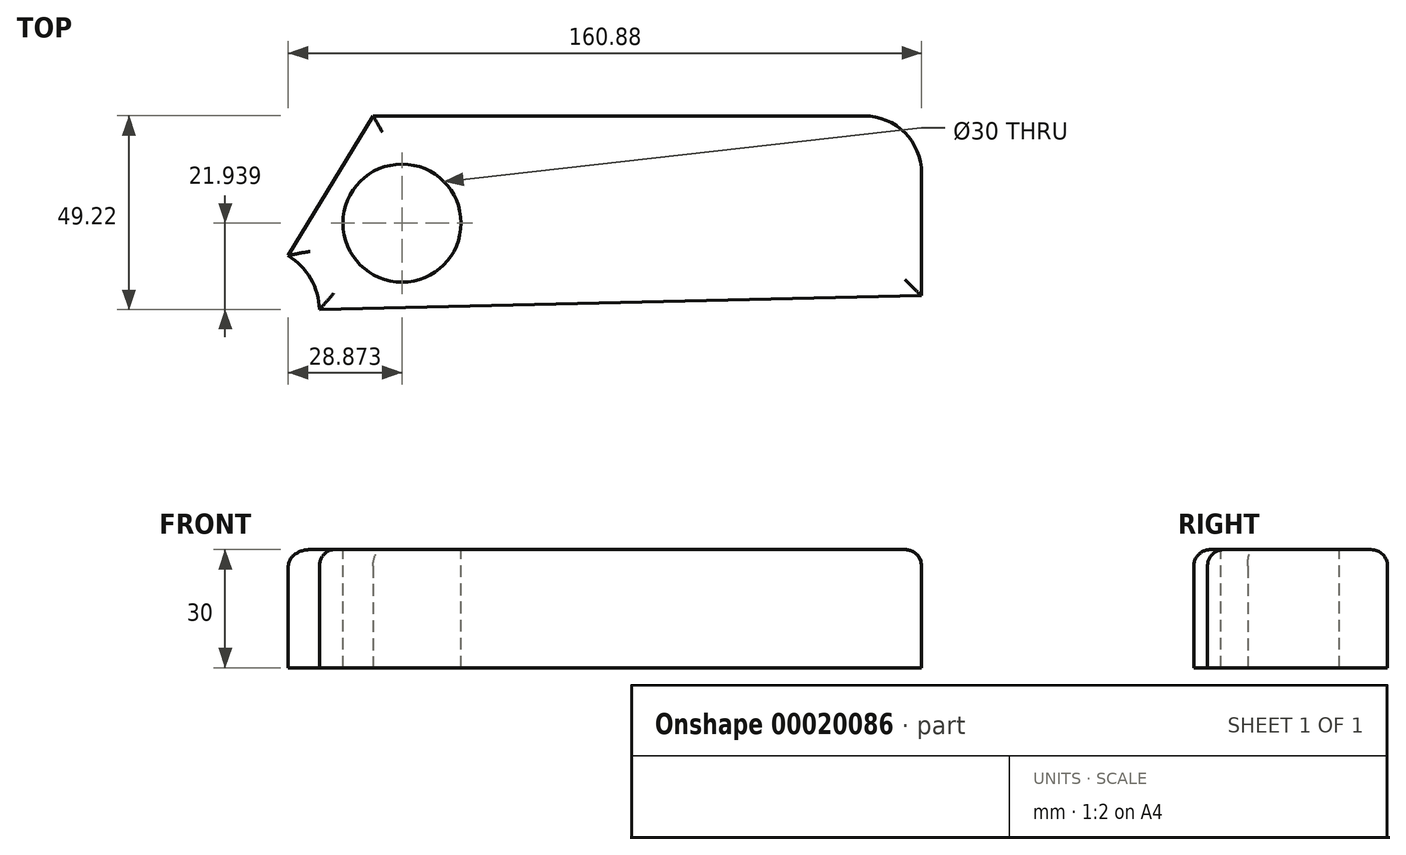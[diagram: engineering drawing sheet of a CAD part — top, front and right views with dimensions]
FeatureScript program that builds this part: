
annotation { "Feature Type Name" : "Feature", "Feature Type Description" : "" }
export const myFeature = defineFeature(function(context is Context, id is Id, definition is map)
    precondition{}
    {
        {
            var Q0;
            Q0=qCreatedBy(makeId("Top.planeOp"),FACE);
            var sketch = newSketch(context, id + "F0", { "sketchPlane" : qUnion([Q0])});
            skLineSegment(sketch, "E0", {"start": v(-103.03, 10.19) * mm, "end": v(-81.49, 45.72) * mm});
            skLineSegment(sketch, "E1", {"start": v(-81.49, 45.72) * mm, "end": v(43.27, 45.72) * mm});
            skLineSegment(sketch, "E2", {"start": v(57.85, 31.13) * mm, "end": v(57.85, 0) * mm});
            skLineSegment(sketch, "E3", {"start": v(57.85, 0) * mm, "end": v(-95.11, -3.5) * mm});
            skArc(sketch, "E4", {"start": v(-95.11, -3.5) * mm, "mid": v(-97.32, 4.36) * mm, "end": v(-103.03, 10.19) * mm});
            skArc(sketch, "E5", {"start": v(57.85, 31.13) * mm, "mid": v(53.58, 41.45) * mm, "end": v(43.27, 45.72) * mm});
            skSolve(sketch);
        }
        {
            var Q0;
            Q0=makeQuery(id+"F0.imprint","IMPRINT",FACE,{"disambiguationData":[TD([[makeQuery(id+"F0.imprint","IMPRINT",EDGE,{"derivedFrom":sQuery(id+"F0.wireOp",EDGE,"E0")}),-1.0]])]});
            extrude(context, id + "F1", {"entities" : qUnion([Q0]), "depth" : 30 * mm});
        }
        {
            var Q0;
            Q0=makeQuery(id+"F1.opExtrude","CAP_FACE",FACE,{"disambiguationData":[OSD([sQuery(id+"F0.wireOp",EDGE,"E0"),sQuery(id+"F0.wireOp",EDGE,"E1"),sQuery(id+"F0.wireOp",EDGE,"E2"),sQuery(id+"F0.wireOp",EDGE,"E3"),sQuery(id+"F0.wireOp",EDGE,"E4"),sQuery(id+"F0.wireOp",EDGE,"E5")])],"isStart":false});
            fillet(context, id + "F2", {"entities" : qUnion([Q0]), "radius" : 4.17 * mm, "tangentPropagation" : true, "allowEdgeOverflow" : false});
        }
        {
            var Q0;
            Q0=makeQuery(id+"F1.opExtrude","CAP_FACE",FACE,{"disambiguationData":[OSD([sQuery(id+"F0.wireOp",EDGE,"E0"),sQuery(id+"F0.wireOp",EDGE,"E1"),sQuery(id+"F0.wireOp",EDGE,"E2"),sQuery(id+"F0.wireOp",EDGE,"E3"),sQuery(id+"F0.wireOp",EDGE,"E4"),sQuery(id+"F0.wireOp",EDGE,"E5")])],"isStart":false});
            var sketch = newSketch(context, id + "F3", { "sketchPlane" : qUnion([Q0])});
            skPoint(sketch, "E6", {"position": v(-74.16, 18.44) * mm});
            skSolve(sketch);
        }
        {
            var Q0;
            Q0=sQuery(id+"F3.wireOp",VERTEX,"E6");
            var Q1;
            Q1=makeQuery(id+"F1.opExtrude","SWEPT_BODY",BODY,{"disambiguationData":[OSD([sQuery(id+"F0.wireOp",EDGE,"E0"),sQuery(id+"F0.wireOp",EDGE,"E1"),sQuery(id+"F0.wireOp",EDGE,"E2"),sQuery(id+"F0.wireOp",EDGE,"E3"),sQuery(id+"F0.wireOp",EDGE,"E4"),sQuery(id+"F0.wireOp",EDGE,"E5")])]});
            hole(context, id + "F4", {"style" : HoleStyle.SIMPLE, "holeDiameter" : 30 * mm, "endStyle" : HoleEndStyle.THROUGH, "locations" : qUnion([Q0]), "scope" : qUnion([Q1])});
        }
    });
